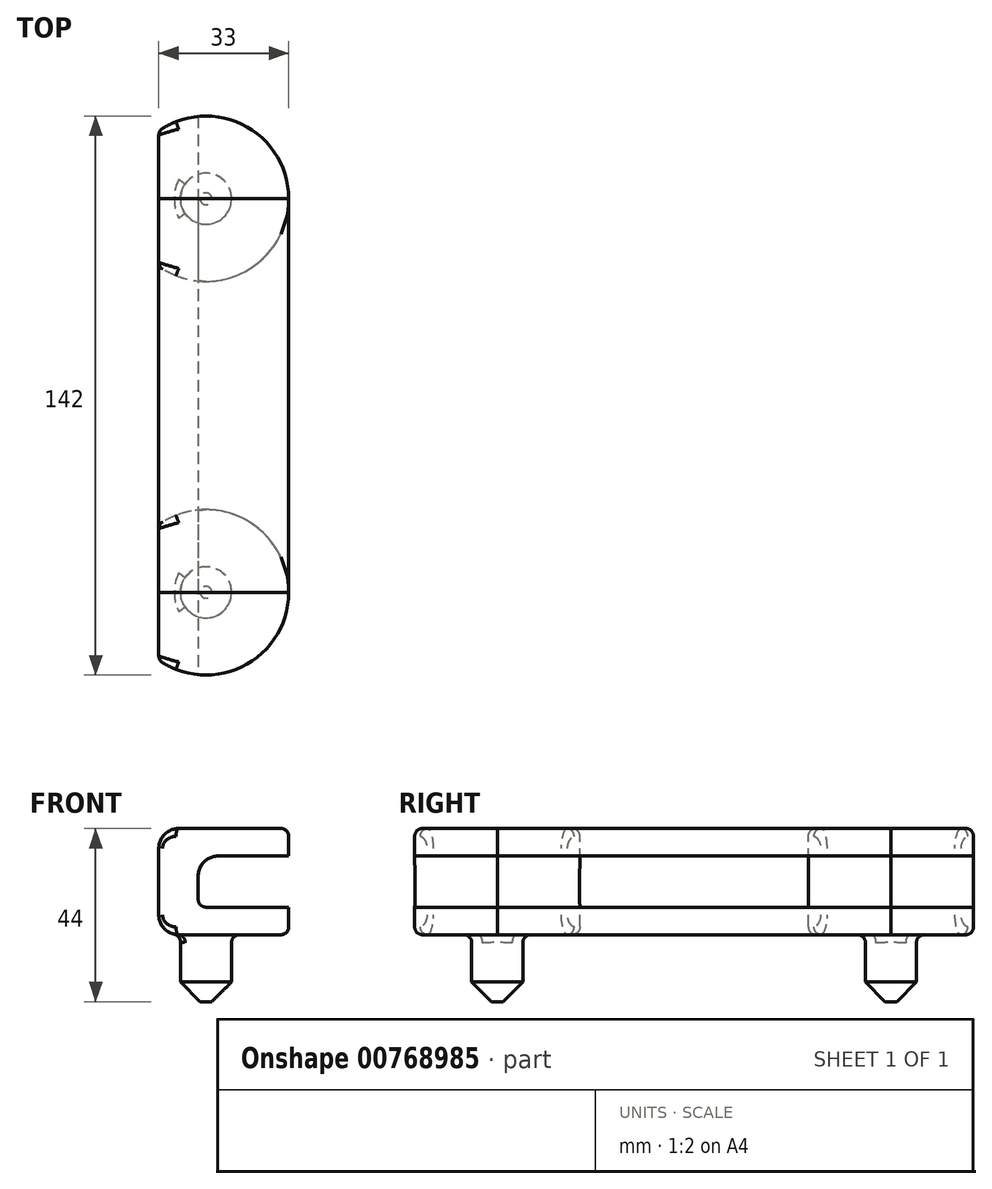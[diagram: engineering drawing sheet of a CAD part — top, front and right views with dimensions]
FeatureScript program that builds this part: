
annotation { "Feature Type Name" : "Feature", "Feature Type Description" : "" }
export const myFeature = defineFeature(function(context is Context, id is Id, definition is map)
    precondition{}
    {
        {
            var Q0;
            Q0=qCreatedBy(makeId("Front.planeOp"),FACE);
            var sketch = newSketch(context, id + "F0", { "sketchPlane" : qUnion([Q0])});
            skLineSegment(sketch, "E0", {"start": v(0, 0) * mm, "end": v(-6.5, 0) * mm});
            skLineSegment(sketch, "E1", {"start": v(-6.5, 0) * mm, "end": v(-6.5, 17) * mm});
            skLineSegment(sketch, "E2", {"start": v(-6.5, 17) * mm, "end": v(-21, 17) * mm});
            skLineSegment(sketch, "E3", {"start": v(-21, 17) * mm, "end": v(-21, 44) * mm});
            skLineSegment(sketch, "E4", {"start": v(-21, 44) * mm, "end": v(0, 44) * mm});
            skLineSegment(sketch, "E5", {"start": v(0, 52.18) * mm, "end": v(0, 44) * mm});
            skLineSegment(sketch, "E6", {"start": v(0, 52.18) * mm, "end": v(0, 0) * mm});
            skSolve(sketch);
        }
        {
            var Q0;
            Q0=makeQuery(id+"F0.imprint","IMPRINT",FACE,{"disambiguationData":[TD([[makeQuery(id+"F0.imprint","IMPRINT",EDGE,{"derivedFrom":sQuery(id+"F0.wireOp",EDGE,"E0")}),-1.0]])]});
            var Q1;
            Q1=sQuery(id+"F0.wireOp",EDGE,"E6");
            revolve(context, id + "F1", {"surfaceOperationType" : NewSurfaceOperationType.NEW, "entities" : qUnion([Q0]), "axis" : qUnion([Q1]), "revolveType" : RevolveType.FULL});
        }
        {
            var Q0;
            Q0=qCreatedBy(makeId("Front.planeOp"),FACE);
            var sketch = newSketch(context, id + "F2", { "sketchPlane" : qUnion([Q0])});
            skLineSegment(sketch, "E7.bottom", {"start": v(-2, 37) * mm, "end": v(50.32, 37) * mm});
            skLineSegment(sketch, "E7.top", {"start": v(-2, 24) * mm, "end": v(50.32, 24) * mm});
            skLineSegment(sketch, "E7.left", {"start": v(-2, 37) * mm, "end": v(-2, 24) * mm});
            skLineSegment(sketch, "E7.right", {"start": v(50.32, 37) * mm, "end": v(50.32, 24) * mm});
            skSolve(sketch);
        }
        {
            var Q0;
            Q0=makeQuery(id+"F2.imprint","IMPRINT",FACE,{"disambiguationData":[TD([[makeQuery(id+"F2.imprint","IMPRINT",EDGE,{"derivedFrom":sQuery(id+"F2.wireOp",EDGE,"E7.bottom")}),-1.0]])]});
            extrude(context, id + "F3", {"entities" : qUnion([Q0]), "operationType" : NewBodyOperationType.REMOVE, "oppositeDirection" : true, "depth" : 35.3 * mm, "offsetDistance" : 25.4 * mm, "hasSecondDirection" : true, "secondDirectionOppositeDirection" : false, "secondDirectionDepth" : 45.47 * mm});
        }
        {
            var Q0;
            Q0=qCreatedBy(makeId("Top.planeOp"),FACE);
            var sketch = newSketch(context, id + "F4", { "sketchPlane" : qUnion([Q0])});
            skLineSegment(sketch, "E8.bottom", {"start": v(-47.92, 40.51) * mm, "end": v(-12, 40.51) * mm});
            skLineSegment(sketch, "E8.top", {"start": v(-47.92, -60.25) * mm, "end": v(-12, -60.25) * mm});
            skLineSegment(sketch, "E8.left", {"start": v(-47.92, 40.51) * mm, "end": v(-47.92, -60.25) * mm});
            skLineSegment(sketch, "E8.right", {"start": v(-12, 40.51) * mm, "end": v(-12, -60.25) * mm});
            skSolve(sketch);
        }
        {
            var Q0;
            Q0=makeQuery(id+"F4.imprint","IMPRINT",FACE,{"disambiguationData":[TD([[makeQuery(id+"F4.imprint","IMPRINT",EDGE,{"derivedFrom":sQuery(id+"F4.wireOp",EDGE,"E8.bottom")}),-1.0]])]});
            extrude(context, id + "F5", {"entities" : qUnion([Q0]), "operationType" : NewBodyOperationType.REMOVE, "depth" : 91.19 * mm, "offsetDistance" : 25.4 * mm});
        }
        {
            var Q0;
            Q0=makeQuery(id+"F1.opRevolve","SWEPT_EDGE",EDGE,{"disambiguationData":[OSD([sQuery(id+"F0.wireOp",EDGE,"E0"),sQuery(id+"F0.wireOp",EDGE,"E1")])]});
            chamfer(context, id + "F6", {"entities" : qUnion([Q0]), "width" : 5 * mm, "tangentPropagation" : true});
        }
        {
            var Q0;
            Q0=qCreatedBy(makeId("Front.planeOp"),FACE);
            var sketch = newSketch(context, id + "F7", { "sketchPlane" : qUnion([Q0])});
            skLineSegment(sketch, "E9", {"start": v(21, 37) * mm, "end": v(21, 44) * mm});
            skLineSegment(sketch, "E10", {"start": v(21, 44) * mm, "end": v(-12, 44) * mm});
            skLineSegment(sketch, "E11", {"start": v(-12, 44) * mm, "end": v(-12, 17) * mm});
            skLineSegment(sketch, "E12", {"start": v(-12, 17) * mm, "end": v(21, 17) * mm});
            skLineSegment(sketch, "E13", {"start": v(21, 17) * mm, "end": v(21, 24) * mm});
            skLineSegment(sketch, "E14", {"start": v(21, 24) * mm, "end": v(-2, 24) * mm});
            skLineSegment(sketch, "E15", {"start": v(-2, 24) * mm, "end": v(-2, 37) * mm});
            skLineSegment(sketch, "E16", {"start": v(-2, 37) * mm, "end": v(21, 37) * mm});
            skSolve(sketch);
        }
        {
            var Q0;
            Q0=qSketchRegion(id+"F7",true);
            extrude(context, id + "F8", {"entities" : qUnion([Q0]), "oppositeDirection" : true, "depth" : 100 * mm, "offsetDistance" : 25 * mm});
        }
        {
            var Q0;
            Q0=makeQuery(id+"F3.boolean.opBoolean","COPY",EDGE,{"derivedFrom":makeQuery(id+"F3.opExtrude","SWEPT_EDGE",EDGE,{"disambiguationData":[OSD([sQuery(id+"F2.wireOp",EDGE,"E7.bottom"),sQuery(id+"F2.wireOp",EDGE,"E7.left")])]})});
            var Q1;
            Q1=makeQuery(id+"F5.boolean.opBoolean","INTERSECT",EDGE,{"derivedFrom":[makeQuery(id+"F1.opRevolve","SWEPT_FACE",FACE,{"disambiguationData":[OSD([sQuery(id+"F0.wireOp",EDGE,"E4")])]}),makeQuery(id+"F5.opExtrude","SWEPT_FACE",FACE,{"disambiguationData":[OSD([sQuery(id+"F4.wireOp",EDGE,"E8.right")])]})]});
            var Q2;
            Q2=makeQuery(id+"F5.boolean.opBoolean","INTERSECT",EDGE,{"derivedFrom":[makeQuery(id+"F1.opRevolve","SWEPT_FACE",FACE,{"disambiguationData":[OSD([sQuery(id+"F0.wireOp",EDGE,"E2")])]}),makeQuery(id+"F5.opExtrude","SWEPT_FACE",FACE,{"disambiguationData":[OSD([sQuery(id+"F4.wireOp",EDGE,"E8.right")])]})]});
            var Q3;
            Q3=makeQuery(id+"F8.opExtrude","SWEPT_EDGE",EDGE,{"disambiguationData":[OSD([sQuery(id+"F7.wireOp",EDGE,"E11"),sQuery(id+"F7.wireOp",EDGE,"E12")])]});
            var Q4;
            Q4=makeQuery(id+"F8.opExtrude","SWEPT_EDGE",EDGE,{"disambiguationData":[OSD([sQuery(id+"F7.wireOp",EDGE,"E10"),sQuery(id+"F7.wireOp",EDGE,"E11")])]});
            var Q5;
            Q5=makeQuery(id+"F8.opExtrude","SWEPT_EDGE",EDGE,{"disambiguationData":[OSD([sQuery(id+"F7.wireOp",EDGE,"E15"),sQuery(id+"F7.wireOp",EDGE,"E16")])]});
            fillet(context, id + "F9", {"entities" : qUnion([Q0, Q1, Q2, Q3, Q4, Q5]), "radius" : 5.08 * mm, "tangentPropagation" : true, "allowEdgeOverflow" : false});
        }
        {
            var Q0;
            Q0=makeQuery(id+"F1.opRevolve","SWEPT_EDGE",EDGE,{"disambiguationData":[OSD([sQuery(id+"F0.wireOp",EDGE,"E3"),sQuery(id+"F0.wireOp",EDGE,"E4")])]});
            var Q1;
            Q1=makeQuery(id+"F1.opRevolve","SWEPT_EDGE",EDGE,{"disambiguationData":[OSD([sQuery(id+"F0.wireOp",EDGE,"E1"),sQuery(id+"F0.wireOp",EDGE,"E2")])]});
            var Q2;
            Q2=makeQuery(id+"F3.boolean.opBoolean","COPY",EDGE,{"derivedFrom":makeQuery(id+"F3.opExtrude","SWEPT_EDGE",EDGE,{"disambiguationData":[OSD([sQuery(id+"F2.wireOp",EDGE,"E7.top"),sQuery(id+"F2.wireOp",EDGE,"E7.left")])]})});
            var Q3;
            Q3=makeQuery(id+"F8.opExtrude","SWEPT_EDGE",EDGE,{"disambiguationData":[OSD([sQuery(id+"F7.wireOp",EDGE,"E9"),sQuery(id+"F7.wireOp",EDGE,"E10")])]});
            var Q4;
            Q4=makeQuery(id+"F8.opExtrude","SWEPT_EDGE",EDGE,{"disambiguationData":[OSD([sQuery(id+"F7.wireOp",EDGE,"E12"),sQuery(id+"F7.wireOp",EDGE,"E13")])]});
            var Q5;
            Q5=makeQuery(id+"F8.opExtrude","SWEPT_EDGE",EDGE,{"disambiguationData":[OSD([sQuery(id+"F7.wireOp",EDGE,"E14"),sQuery(id+"F7.wireOp",EDGE,"E15")])]});
            fillet(context, id + "F10", {"entities" : qUnion([Q0, Q1, Q2, Q3, Q4, Q5]), "radius" : 2 * mm, "tangentPropagation" : true, "allowEdgeOverflow" : false});
        }
        {
            var Q0;
            Q0=makeQuery(id+"F1.opRevolve","SWEPT_BODY",BODY,{"disambiguationData":[OSD([sQuery(id+"F0.wireOp",EDGE,"E0"),sQuery(id+"F0.wireOp",EDGE,"E1"),sQuery(id+"F0.wireOp",EDGE,"E2"),sQuery(id+"F0.wireOp",EDGE,"E3"),sQuery(id+"F0.wireOp",EDGE,"E4"),sQuery(id+"F0.wireOp",EDGE,"E5"),sQuery(id+"F0.wireOp",EDGE,"E6")])]});
            transform(context, id + "F11", {"entities" : qUnion([Q0]), "transformType" : TransformType.TRANSLATION_3D, "dx" : 0 * mm, "dy" : 100 * mm, "dz" : 0 * mm, "makeCopy" : true});
        }
    });
